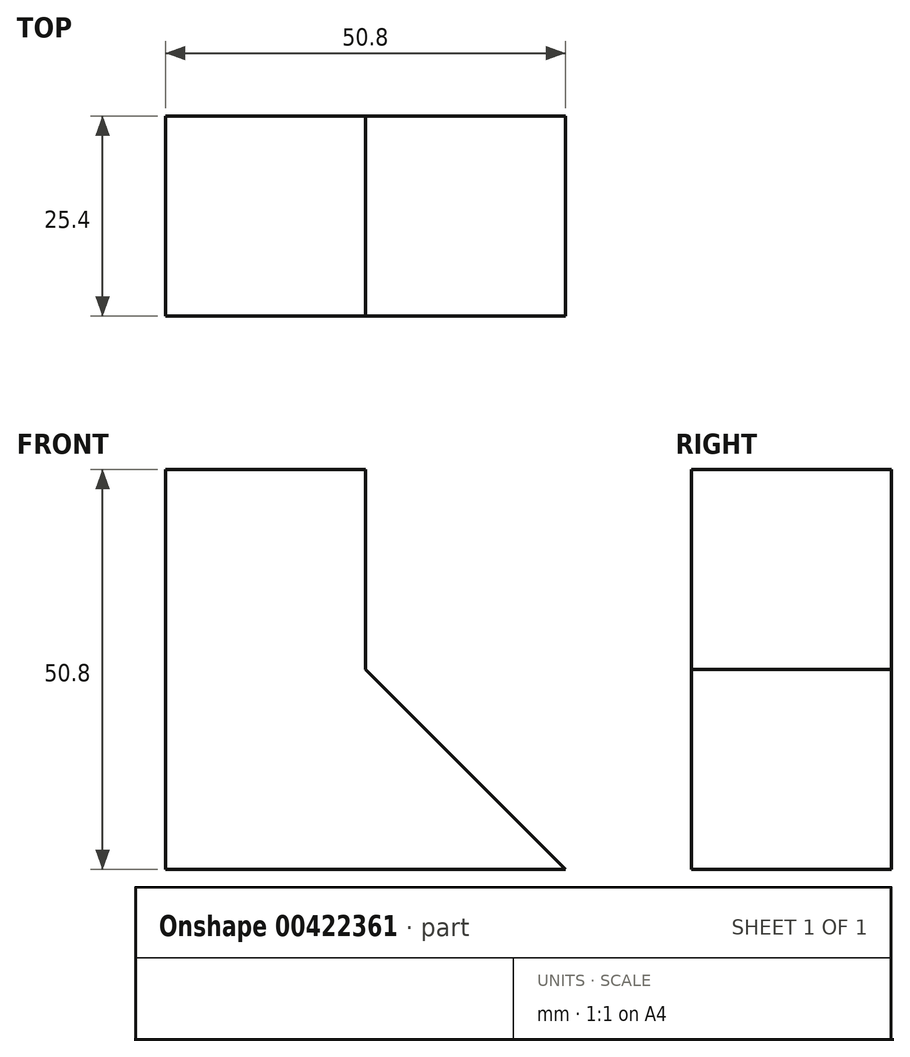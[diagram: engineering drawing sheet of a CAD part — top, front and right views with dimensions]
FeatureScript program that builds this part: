
annotation { "Feature Type Name" : "Feature", "Feature Type Description" : "" }
export const myFeature = defineFeature(function(context is Context, id is Id, definition is map)
    precondition{}
    {
        {
            var Q0;
            Q0=qCreatedBy(makeId("Front.planeOp"),FACE);
            var sketch = newSketch(context, id + "F0", { "sketchPlane" : qUnion([Q0])});
            skLineSegment(sketch, "E0", {"start": v(-50.8, 10.24) * mm, "end": v(-50.8, -40.56) * mm});
            skLineSegment(sketch, "E1", {"start": v(-50.8, -40.56) * mm, "end": v(0, -40.56) * mm});
            skLineSegment(sketch, "E2", {"start": v(-50.8, 10.24) * mm, "end": v(-25.4, 10.24) * mm});
            skLineSegment(sketch, "E3", {"start": v(-25.4, 10.24) * mm, "end": v(-25.4, -15.16) * mm});
            skLineSegment(sketch, "E4", {"start": v(-25.4, -15.16) * mm, "end": v(0, -40.56) * mm});
            skSolve(sketch);
        }
        {
            var Q0;
            Q0 = qSketchRegion(id + "F0", true);
            extrude(context, id + "F1", {"entities" : qUnion([Q0]), "depth" : 25.4 * mm});
        }
    });
